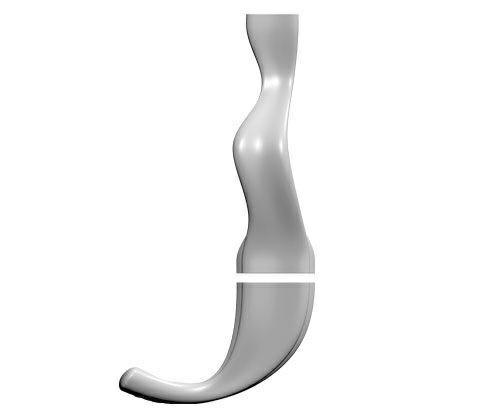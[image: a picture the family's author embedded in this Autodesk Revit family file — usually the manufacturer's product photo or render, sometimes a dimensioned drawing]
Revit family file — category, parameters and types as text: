
# Revit family: CITY ALPHABET litera „J”
name_source: partatom
category: Meble
revit_build: Autodesk Revit 2018 (Build: 20190510_1515(x64)
units: mm (PartAtom-declared; Revit-internal decimal feet)

## family parameters
Numer OmniClass = 23.40.10.11.14
Obiekt nadrzędny = Powierzchnia
Punkt obliczania pomieszczeń = Nie
Tnij formami wycięć po wczytaniu = Nie
Tytuł OmniClass = Exterior Seating
Współdzielony = Nie

## types (1)
- CITY ALPHABET litera „J”
    Domyślna rzędna = 1219 mm
    Długość = 3600 mm  [stored 11.811 ft]
    IfcExportAs = IfcFurnishingElement
    Komentarze do typu = Ławka
    Materiał - informacja = Szeroki wybór kolorów wg palety RAL. Istnieje również możliwość specjalnego wykonania
kolorystycznego na indywidualne zapytanie klienta.
    Model = CITY ALPHABET litera „J”
    Obraz typu = J.jpg
    Producent = Astrini Design
    Szerokość = 1800 mm  [stored 5.90551 ft]
    Temepratura użytkowania = -40°C do 80°C, ( -40°F do 176°F )
    URL = http://astrini-design.pl
    Waga (szacunkowo) = 61.00 kg
    Waga po wypełnieniu (szacunkowo) = 161.00 kg
    Wysokość = 600 mm

note: [stored X ft] marks values corroborated as IEEE doubles in the binary element streams (Revit-internal decimal feet)
